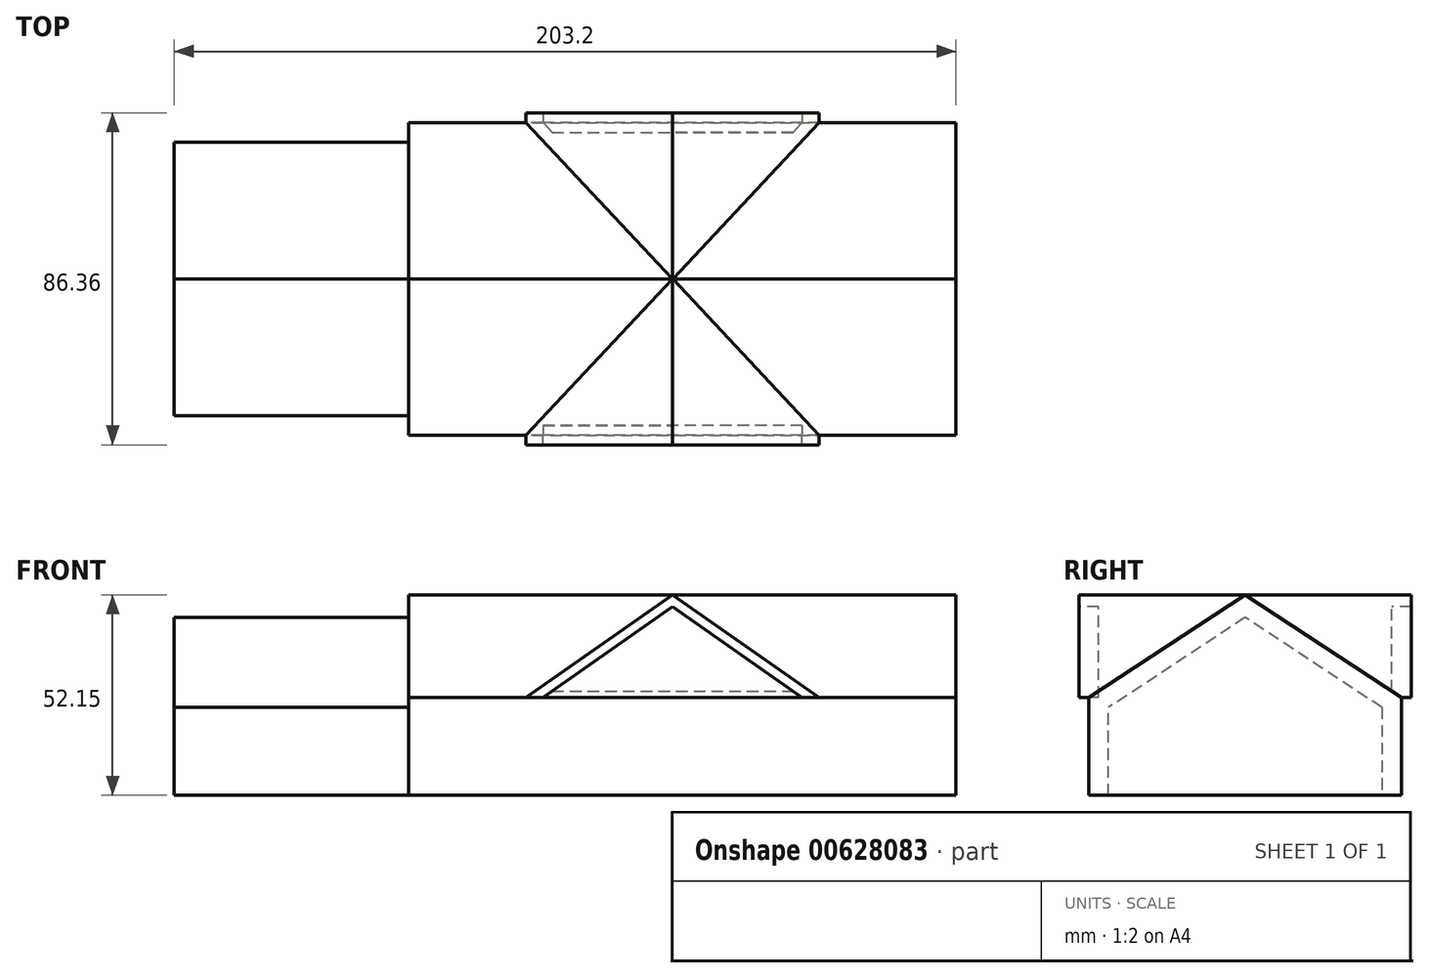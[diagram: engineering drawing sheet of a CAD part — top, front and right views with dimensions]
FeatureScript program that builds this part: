
annotation { "Feature Type Name" : "Feature", "Feature Type Description" : "" }
export const myFeature = defineFeature(function(context is Context, id is Id, definition is map)
    precondition{}
    {
        {
            var Q0;
            Q0=qCreatedBy(makeId("Front.planeOp"),FACE);
            var sketch = newSketch(context, id + "F0", { "sketchPlane" : qUnion([Q0])});
            skLineSegment(sketch, "E0", {"start": v(-116.09, -26.54) * mm, "end": v(87.11, -26.54) * mm});
            skLineSegment(sketch, "E1", {"start": v(87.11, -26.54) * mm, "end": v(87.11, -1.14) * mm});
            skLineSegment(sketch, "E2", {"start": v(87.11, -1.14) * mm, "end": v(-116.09, -1.14) * mm});
            skLineSegment(sketch, "E3", {"start": v(-116.09, -1.14) * mm, "end": v(-116.09, -26.54) * mm});
            skSolve(sketch);
        }
        {
            var Q0;
            Q0=makeQuery(id+"F0.imprint","IMPRINT",FACE,{"disambiguationData":[TD([[makeQuery(id+"F0.imprint","IMPRINT",EDGE,{"derivedFrom":sQuery(id+"F0.wireOp",EDGE,"E0")}),1.0]])]});
            extrude(context, id + "F1", {"entities" : qUnion([Q0]), "oppositeDirection" : true, "depth" : 81.28 * mm, "offsetDistance" : 25.4 * mm});
        }
        {
            var Q0;
            Q0=makeQuery(id+"F1.opExtrude","SWEPT_FACE",FACE,{"disambiguationData":[OSD([sQuery(id+"F0.wireOp",EDGE,"E1")])]});
            var sketch = newSketch(context, id + "F2", { "sketchPlane" : qUnion([Q0])});
            skLineSegment(sketch, "E4", {"start": v(81.28, -1.14) * mm, "end": v(40.64, 25.55) * mm});
            skPoint(sketch, "E4.endSnap0", {"position": v(40.64, -1.14) * mm});
            skLineSegment(sketch, "E5", {"start": v(40.64, 25.55) * mm, "end": v(0, -1.14) * mm});
            skLineSegment(sketch, "E6", {"start": v(0, -1.14) * mm, "end": v(81.28, -1.14) * mm});
            skSolve(sketch);
        }
        {
            var Q0;
            Q0=makeQuery(id+"F2.imprint","IMPRINT",FACE,{"disambiguationData":[TD([[makeQuery(id+"F2.imprint","IMPRINT",EDGE,{"derivedFrom":sQuery(id+"F2.wireOp",EDGE,"E4")}),1.0]])]});
            extrude(context, id + "F3", {"entities" : qUnion([Q0]), "operationType" : NewBodyOperationType.ADD, "oppositeDirection" : true, "depth" : 203.2 * mm, "offsetDistance" : 25.4 * mm});
        }
        {
            var Q0;
            Q0=makeQuery(id+"F1.opExtrude","CAP_FACE",FACE,{"disambiguationData":[OSD([sQuery(id+"F0.wireOp",EDGE,"E0"),sQuery(id+"F0.wireOp",EDGE,"E1"),sQuery(id+"F0.wireOp",EDGE,"E2"),sQuery(id+"F0.wireOp",EDGE,"E3")])],"isStart":true});
            var sketch = newSketch(context, id + "F4", { "sketchPlane" : qUnion([Q0])});
            skPoint(sketch, "E7", {"position": v(-24.65, -1.14) * mm});
            skPoint(sketch, "E8", {"position": v(51.55, -1.14) * mm});
            skLineSegment(sketch, "E9", {"start": v(-24.65, -1.14) * mm, "end": v(51.55, -1.14) * mm});
            skPoint(sketch, "E10", {"position": v(13.45, 25.6) * mm});
            skPoint(sketch, "E10.positionSnap0", {"position": v(13.45, -1.14) * mm});
            skLineSegment(sketch, "E11", {"start": v(-24.65, -1.14) * mm, "end": v(13.45, 25.6) * mm});
            skLineSegment(sketch, "E12", {"start": v(51.55, -1.14) * mm, "end": v(13.45, 25.6) * mm});
            skLineSegment(sketch, "E13.0", {"start": v(-20.23, -1.14) * mm, "end": v(13.45, 22.5) * mm});
            skLineSegment(sketch, "E13.1", {"start": v(47.13, -1.14) * mm, "end": v(13.45, 22.5) * mm});
            skSolve(sketch);
        }
        {
            var Q0;
            {var subQ1=sQuery(id+"F4.wireOp",EDGE,"E11");Q0=makeQuery(id+"F4.imprint","IMPRINT",FACE,{"disambiguationData":[TD([[makeQuery(id+"F4.imprint","IMPRINT",EDGE,{"derivedFrom":subQ1}),-1.0]])]});}
            extrude(context, id + "F5", {"entities" : qUnion([Q0]), "operationType" : NewBodyOperationType.ADD, "oppositeDirection" : true, "depth" : 83.82 * mm, "offsetDistance" : 25.4 * mm});
        }
        {
            var Q0;
            {var subQ0=sQuery(id+"F4.wireOp",EDGE,"E13.0");Q0=makeQuery(id+"F4.imprint","IMPRINT",FACE,{"disambiguationData":[TD([[makeQuery(id+"F4.imprint","IMPRINT",EDGE,{"derivedFrom":subQ0}),-1.0]])]});}
            extrude(context, id + "F6", {"entities" : qUnion([Q0]), "operationType" : NewBodyOperationType.ADD, "oppositeDirection" : true, "depth" : 78.74 * mm, "offsetDistance" : 25.4 * mm});
        }
        {
            var Q0;
            {var subQ0=sQuery(id+"F4.wireOp",EDGE,"E13.0");Q0=makeQuery(id+"F4.imprint","IMPRINT",FACE,{"disambiguationData":[TD([[makeQuery(id+"F4.imprint","IMPRINT",EDGE,{"derivedFrom":subQ0}),-1.0]])]});}
            extrude(context, id + "F7", {"entities" : qUnion([Q0]), "operationType" : NewBodyOperationType.REMOVE, "oppositeDirection" : true, "depth" : 2.54 * mm, "offsetDistance" : 25.4 * mm});
        }
        {
            var Q0;
            {var subQ1=sQuery(id+"F4.wireOp",EDGE,"E11");Q0=makeQuery(id+"F4.imprint","IMPRINT",FACE,{"disambiguationData":[TD([[makeQuery(id+"F4.imprint","IMPRINT",EDGE,{"derivedFrom":subQ1}),-1.0]])]});}
            extrude(context, id + "F8", {"entities" : qUnion([Q0]), "operationType" : NewBodyOperationType.ADD, "depth" : 2.54 * mm, "offsetDistance" : 25.4 * mm});
        }
        {
            var Q0;
            Q0=makeQuery(id+"F3.boolean.opBoolean","MERGE",FACE,{"derivedFrom":[makeQuery(id+"F1.opExtrude","SWEPT_FACE",FACE,{"disambiguationData":[OSD([sQuery(id+"F0.wireOp",EDGE,"E3")])]}),makeQuery(id+"F3.opExtrude","CAP_FACE",FACE,{"disambiguationData":[OSD([sQuery(id+"F2.wireOp",EDGE,"E4"),sQuery(id+"F2.wireOp",EDGE,"E5"),sQuery(id+"F2.wireOp",EDGE,"E6")])],"isStart":false})]});
            extrude(context, id + "F9", {"entities" : qUnion([Q0]), "operationType" : NewBodyOperationType.REMOVE, "oppositeDirection" : true, "depth" : 60.96 * mm, "offsetDistance" : 25.4 * mm});
        }
        {
            var Q0;
            Q0=makeQuery(id+"F9.boolean.opBoolean","COPY",FACE,{"derivedFrom":makeQuery(id+"F9.opExtrude","CAP_FACE",FACE,{"disambiguationData":[OSD([sQuery(id+"F0.wireOp",EDGE,"E3"),sQuery(id+"F2.wireOp",EDGE,"E4"),sQuery(id+"F2.wireOp",EDGE,"E5"),sQuery(id+"F2.wireOp",EDGE,"E6")])],"isStart":false})});
            var sketch = newSketch(context, id + "F10", { "sketchPlane" : qUnion([Q0])});
            skPoint(sketch, "E14", {"position": v(-76.2, -26.54) * mm});
            skPoint(sketch, "E15", {"position": v(-5.08, -26.54) * mm});
            skPoint(sketch, "E16", {"position": v(-5.08, -3.68) * mm});
            skPoint(sketch, "E17", {"position": v(-76.2, -3.68) * mm});
            skLineSegment(sketch, "E18", {"start": v(-76.2, -3.68) * mm, "end": v(-76.2, -26.54) * mm});
            skLineSegment(sketch, "E19", {"start": v(-5.08, -26.54) * mm, "end": v(-5.08, -3.68) * mm});
            skLineSegment(sketch, "E20", {"start": v(-76.2, -26.54) * mm, "end": v(-5.08, -26.54) * mm});
            skLineSegment(sketch, "E21", {"start": v(-76.2, -3.68) * mm, "end": v(-40.64, 19.68) * mm});
            skLineSegment(sketch, "E22", {"start": v(-40.64, 19.68) * mm, "end": v(-5.08, -3.68) * mm});
            skSolve(sketch);
        }
        {
            var Q0;
            Q0=makeQuery(id+"F10.imprint","IMPRINT",FACE,{"disambiguationData":[TD([[makeQuery(id+"F10.imprint","IMPRINT",EDGE,{"derivedFrom":sQuery(id+"F10.wireOp",EDGE,"E18")}),1.0]])]});
            extrude(context, id + "F11", {"entities" : qUnion([Q0]), "operationType" : NewBodyOperationType.ADD, "depth" : 60.96 * mm, "offsetDistance" : 25.4 * mm});
        }
    });
